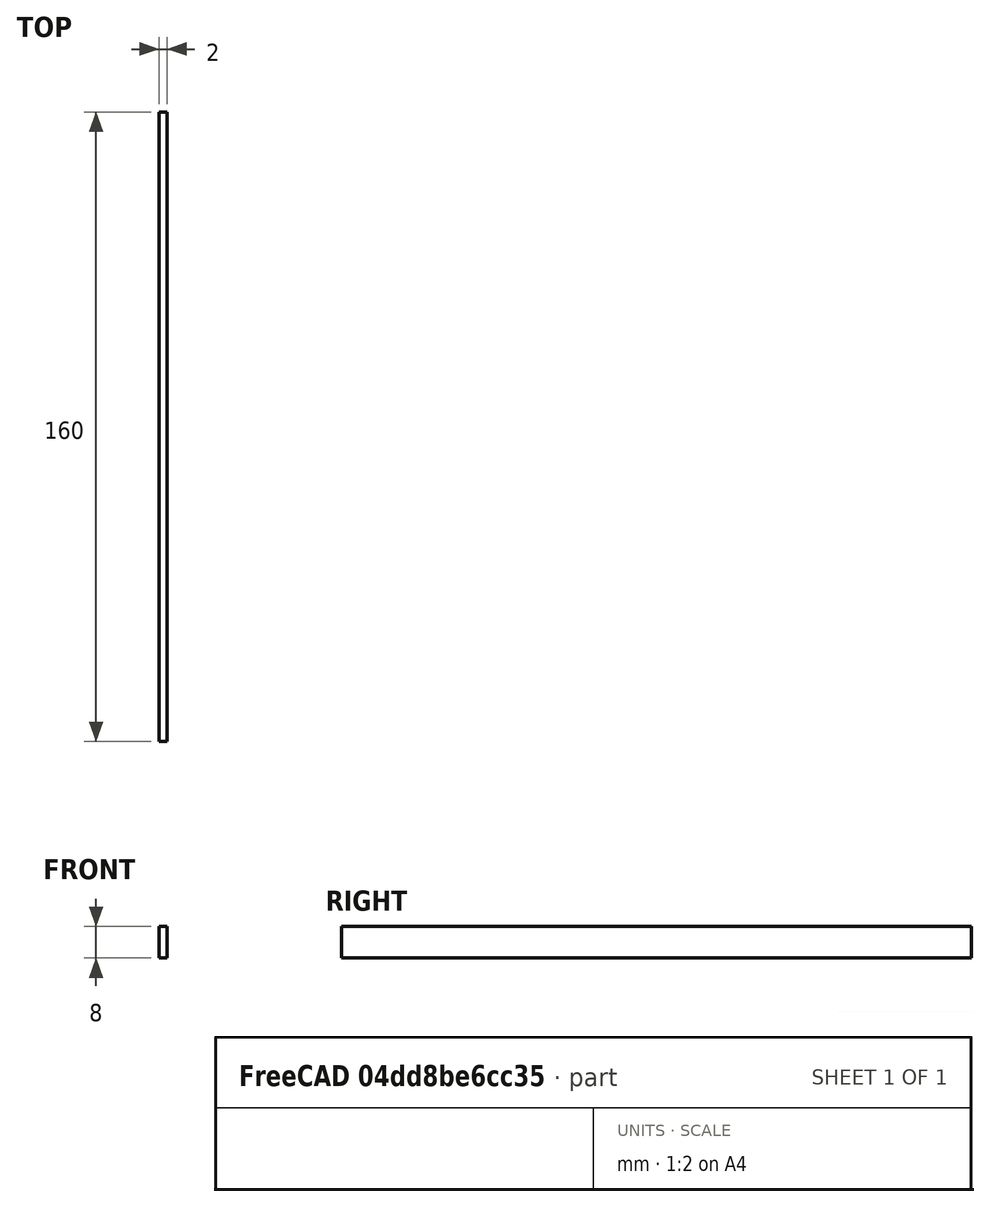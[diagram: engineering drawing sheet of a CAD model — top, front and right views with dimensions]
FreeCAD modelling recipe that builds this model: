
FCSTD DOCUMENT  (FreeCAD 1.0R39285 (Git))
Label: Framerail
License: All rights reserved
LicenseURL: https://en.wikipedia.org/wiki/All_rights_reserved
objects: App::Link×2, Sketcher::SketchObject×1, PartDesign::Pad×1, PartDesign::Body×1
note: 6 computed .brp shape members not serialized (recipe doc carries the construction recipe); baked Part::Feature solids carry a one-line shape summary decoded from their .brp
EXTERNAL_REF file=../../Dimentions.FCStd obj=Spreadsheet
EXTERNAL_REF file=../../Dimentions.FCStd obj=dd005

FEATURE [Sketcher::SketchObject] Sketch
  ArcFitTolerance = 1e-06
  AttachmentSupport = -> [YZ_Plane]
  FullyConstrained = true
  MakeInternals = false
  MapMode = 5
  Placement = pos=(0,0,0) rot=(0.57735,0.57735,0.57735;2.0944rad)
  expr: .Constraints.FrameRailHeight = <<General>>.FrameRailHeight
  expr: .Constraints.FrameRailLength = <<Frame>>.Length
  sketch-geometry (4):
    g0: LineSegment StartX=-80 StartY=4 StartZ=0 EndX=-80 EndY=-4 EndZ=0
    g1: LineSegment StartX=-80 StartY=-4 StartZ=0 EndX=80 EndY=-4 EndZ=0
    g2: LineSegment StartX=80 StartY=-4 StartZ=0 EndX=80 EndY=4 EndZ=0
    g3: LineSegment StartX=80 StartY=4 StartZ=0 EndX=-80 EndY=4 EndZ=0
  constraints (10):
    c: Coincident(g0,g1)
    c: Coincident(g1,g2)
    c: Coincident(g2,g3)
    c: Coincident(g3,g0)
    c: Vertical(g0)
    c: Horizontal(g1)
    c: Symmetric(g1,g2,g-1)
    c: Symmetric(g0,g2,g-2)
    c: DistanceX(g3,g3) = 160  'FrameRailLength'
    c: Distance(g2,g2) = 8  'FrameRailHeight'
FEATURE [App::Link] Link  label="General"
  LinkedObject = -> <external ../../Dimentions.FCStd>#Spreadsheet
FEATURE [PartDesign::Pad] Pad
  Direction = (1,0,0)
  Length = 2
  Length2 = 10
  Midplane = true
  Placement = pos=(0,0,0) rot=(1,1,1;2.0944rad)
  Profile = -> Sketch
  ReferenceAxis = -> Sketch [N_Axis]
  Refine = true
  Suppressed = false
  Type = 0
  expr: Length = <<General>>.FrameRailThickness
FEATURE [PartDesign::Body] Body  label="Framerail"
  AllowCompound = false
  Group = -> [Sketch,Pad]
  Origin = -> Origin
  Tip = -> Pad
FEATURE [App::Link] Link001  label="Frame"
  CrossMemberHeight = 8
  LinkedObject = -> <external ../../Dimentions.FCStd>#dd005
  Width = 10
